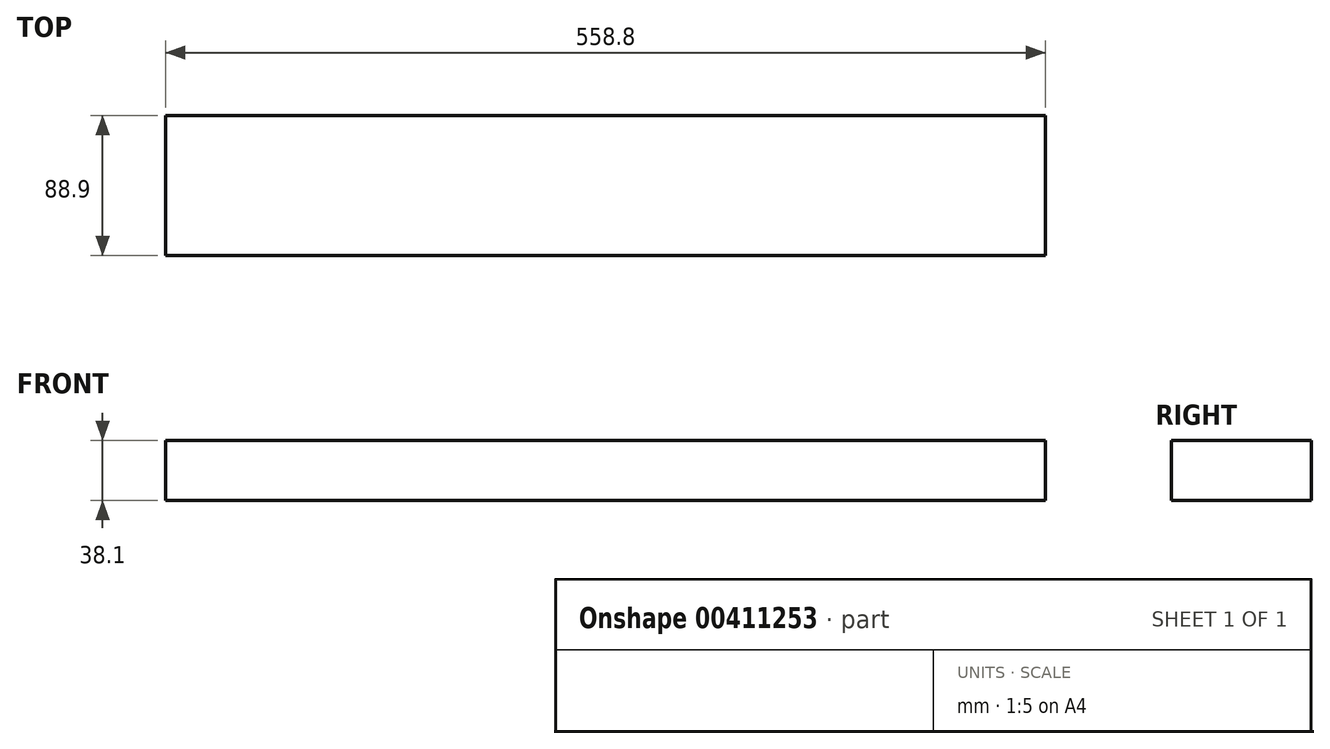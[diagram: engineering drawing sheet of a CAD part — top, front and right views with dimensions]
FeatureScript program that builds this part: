
annotation { "Feature Type Name" : "Feature", "Feature Type Description" : "" }
export const myFeature = defineFeature(function(context is Context, id is Id, definition is map)
    precondition{}
    {
        {
            var Q0;
            Q0=qCreatedBy(makeId("Right.planeOp"),FACE);
            var sketch = newSketch(context, id + "F0", { "sketchPlane" : qUnion([Q0])});
            skLineSegment(sketch, "E0.bottom", {"start": v(44.45, -19.05) * mm, "end": v(-44.45, -19.05) * mm});
            skLineSegment(sketch, "E0.top", {"start": v(44.45, 19.05) * mm, "end": v(-44.45, 19.05) * mm});
            skLineSegment(sketch, "E0.left", {"start": v(44.45, -19.05) * mm, "end": v(44.45, 19.05) * mm});
            skLineSegment(sketch, "E0.right", {"start": v(-44.45, -19.05) * mm, "end": v(-44.45, 19.05) * mm});
            skPoint(sketch, "E0.middle", {"position": v(0, 0) * mm});
            skSolve(sketch);
        }
        {
            var Q0;
            Q0=makeQuery(id+"F0.imprint","IMPRINT",FACE,{"disambiguationData":[TD([[makeQuery(id+"F0.imprint","IMPRINT",EDGE,{"derivedFrom":sQuery(id+"F0.wireOp",EDGE,"E0.bottom")}),-1.0]])]});
            extrude(context, id + "F1", {"entities" : qUnion([Q0]), "depth" : 279.4 * mm, "hasSecondDirection" : true, "secondDirectionOppositeDirection" : true, "secondDirectionDepth" : 279.4 * mm});
        }
    });
